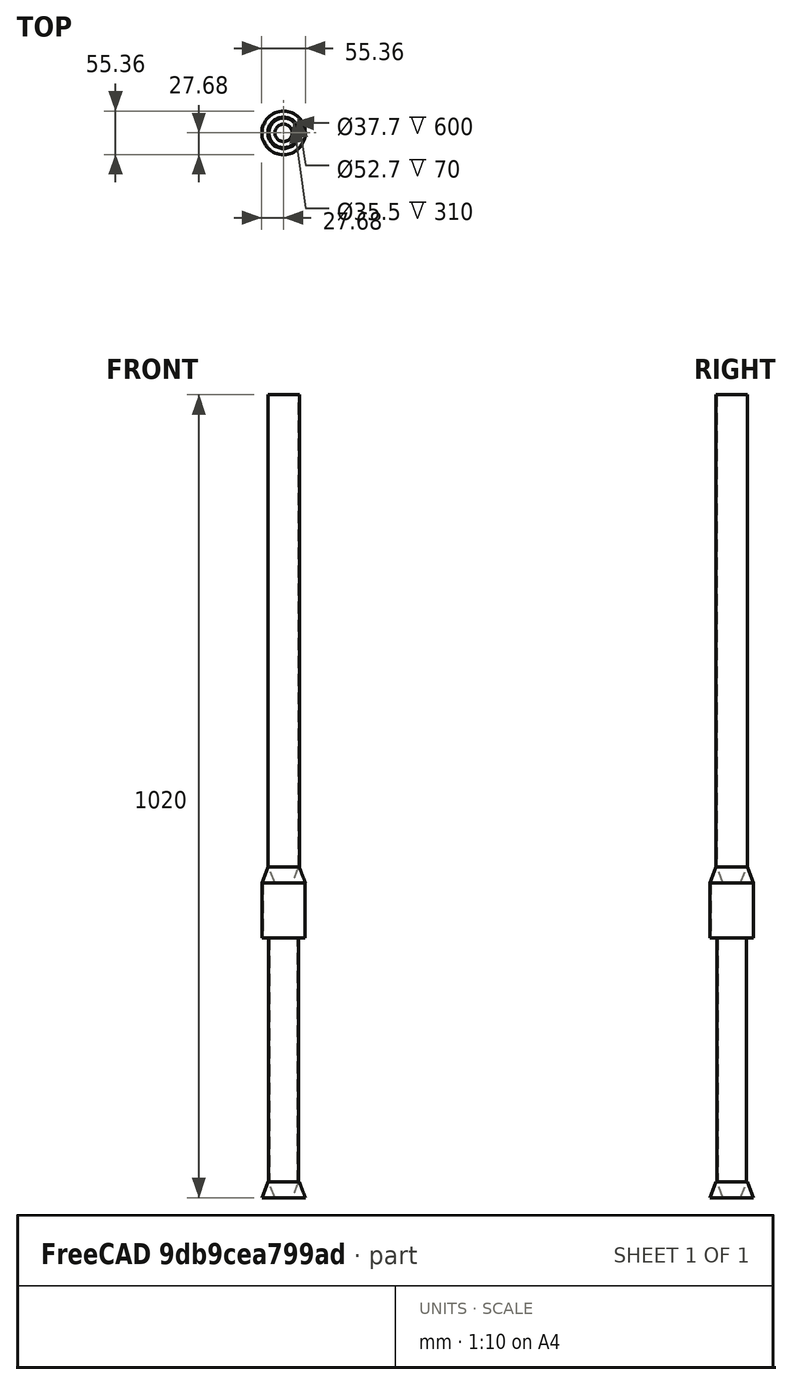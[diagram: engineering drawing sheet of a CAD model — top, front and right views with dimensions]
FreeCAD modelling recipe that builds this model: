
FCSTD DOCUMENT  (FreeCAD 0.21R33771 (Git))
Label: CaneDesign3
License: All rights reserved
LicenseURL: https://en.wikipedia.org/wiki/All_rights_reserved
objects: PartDesign::Body×6, Sketcher::SketchObject×5, PartDesign::Pad×5, App::MeasureDistance×3, Mesh::Feature×1, Spreadsheet::Sheet×1
note: 21 computed .brp shape members not serialized (recipe doc carries the construction recipe); baked Part::Feature solids carry a one-line shape summary decoded from their .brp

FEATURE [Sketcher::SketchObject] Sketch
  FullyConstrained = true
  MapMode = 5
  Support = -> [XY_Plane]
  sketch-geometry (2):
    g0: Circle CenterX=0 CenterY=0 CenterZ=0 NormalX=0 NormalY=0 NormalZ=1 AngleXU=0 Radius=18.9
    g1: Circle CenterX=0 CenterY=0 CenterZ=0 NormalX=0 NormalY=0 NormalZ=1 AngleXU=0 Radius=17.75
  constraints (4):
    c: Coincident(g0,g-1)
    c: Diameter(g0) = 37.8
    c: Coincident(g1,g0)
    c: Diameter(g1) = 35.5
FEATURE [PartDesign::Pad] Pad
  Direction = (0,0,1)
  Length = 310
  Length2 = 10
  Profile = -> Sketch
  ReferenceAxis = -> Sketch [N_Axis]
  Type = 0
FEATURE [PartDesign::Body] Body  label="LegShaft"
  Group = -> [Sketch,Pad]
  Origin = -> Origin
  Placement = pos=(0,0,-160) rot=(0,0,1;0rad)
  Tip = -> Pad
  expr: .Placement.Base.z = <<parameters>>.adjustment_positionz
FEATURE [Sketcher::SketchObject] Sketch001
  FullyConstrained = false
  MapMode = 5
  Support = -> [XY_Plane001]
  sketch-geometry (2):
    g0: Circle CenterX=0 CenterY=0 CenterZ=0 NormalX=0 NormalY=0 NormalZ=1 AngleXU=0 Radius=20
    g1: Circle CenterX=0 CenterY=0 CenterZ=0 NormalX=0 NormalY=0 NormalZ=1 AngleXU=0 Radius=18.85
  constraints (3):
    c: Diameter(g0) = 40
    c: Coincident(g1,g0)
    c: Diameter(g1) = 37.7
FEATURE [PartDesign::Pad] Pad001
  Direction = (0,0,1)
  Length = 600
  Length2 = 10
  Profile = -> Sketch001
  ReferenceAxis = -> Sketch001 [N_Axis]
  Type = 0
FEATURE [PartDesign::Body] Body001  label="ProtectiveCover"
  Group = -> [Sketch001,Pad001]
  Origin = -> Origin001
  Placement = pos=(0,0,240) rot=(0,20,0;0rad)
  Tip = -> Pad001
  expr: .Placement.Rotation.Axis.y = 20
FEATURE [Sketcher::SketchObject] Sketch002
  FullyConstrained = true
  MapMode = 5
  Support = -> [XY_Plane002]
  sketch-geometry (2):
    g0: Circle CenterX=0 CenterY=0 CenterZ=0 NormalX=0 NormalY=0 NormalZ=1 AngleXU=0 Radius=27.5
    g1: Circle CenterX=0 CenterY=0 CenterZ=0 NormalX=0 NormalY=0 NormalZ=1 AngleXU=0 Radius=26.35
  constraints (4):
    c: Coincident(g0,g-1)
    c: Diameter(g0) = 55
    c: Coincident(g1,g0)
    c: Diameter(g1) = 52.7
FEATURE [PartDesign::Pad] Pad002
  Direction = (0,0,1)
  Length = 70
  Length2 = 10
  Profile = -> Sketch002
  ReferenceAxis = -> Sketch002 [N_Axis]
  Type = 0
FEATURE [PartDesign::Body] Body002  label="MotorCover"
  Group = -> [Sketch002,Pad002]
  Origin = -> Origin002
  Placement = pos=(0,0,150) rot=(0,0,1;0rad)
  Tip = -> Pad002
FEATURE [Sketcher::SketchObject] Sketch003
  FullyConstrained = true
  MapMode = 5
  Support = -> [XY_Plane003]
  sketch-geometry (2):
    g0: Circle CenterX=0 CenterY=0 CenterZ=0 NormalX=0 NormalY=0 NormalZ=1 AngleXU=0 Radius=20
    g1: Circle CenterX=0 CenterY=0 CenterZ=0 NormalX=0 NormalY=0 NormalZ=1 AngleXU=0 Radius=18.75
  constraints (4):
    c: Coincident(g0,g-1)
    c: Diameter(g0) = 40
    c: Coincident(g1,g0)
    c: Diameter(g1) = 37.5
FEATURE [PartDesign::Pad] Pad003
  Direction = (0,0,1)
  Length = 20
  Length2 = 10
  Profile = -> Sketch003
  ReferenceAxis = -> Sketch003 [N_Axis]
  Reversed = true
  TaperAngle = 21
  Type = 0
FEATURE [PartDesign::Body] Body003  label="MotorCoverTransition"
  Group = -> [Sketch003,Pad003]
  Origin = -> Origin003
  Placement = pos=(0,0,240) rot=(0,0,1;0rad)
  Tip = -> Pad003
FEATURE [PartDesign::Body] Body004  label="Body"
  Origin = -> Origin004
FEATURE [Mesh::Feature] _7097_Cane_flat_handle_v1_NEW  label="17097_Cane_flat_handle_v1_NEW"
  Placement = pos=(7,10,-69) rot=(0,0,1;1.5708rad)
FEATURE [Sketcher::SketchObject] Sketch005
  FullyConstrained = true
  MapMode = 5
  Support = -> [XY_Plane006]
  sketch-geometry (2):
    g0: Circle CenterX=0 CenterY=0 CenterZ=0 NormalX=0 NormalY=0 NormalZ=1 AngleXU=0 Radius=20
    g1: Circle CenterX=0 CenterY=0 CenterZ=0 NormalX=0 NormalY=0 NormalZ=1 AngleXU=0 Radius=18.75
  constraints (4):
    c: Coincident(g0,g-1)
    c: Diameter(g0) = 40
    c: Coincident(g1,g0)
    c: Diameter(g1) = 37.5
FEATURE [PartDesign::Pad] Pad005
  Direction = (0,0,1)
  Length = 20
  Length2 = 10
  Profile = -> Sketch005
  ReferenceAxis = -> Sketch005 [N_Axis]
  Reversed = true
  TaperAngle = 21
  Type = 0
FEATURE [PartDesign::Body] Body006  label="Foot"
  Group = -> [Sketch005,Pad005]
  Origin = -> Origin006
  Placement = pos=(0,0,-160) rot=(0,0,1;0rad)
  Tip = -> Pad005
  expr: .Placement.Base.z = <<parameters>>.adjustment_positionz
FEATURE [App::MeasureDistance] Distance  label="Distance: 600.16 mm"
  Distance = 600.161
  P1 = (20,0,840)
  P2 = (20.062,0,239.839)
FEATURE [App::MeasureDistance] Distance001  label="Distance: 89.91 mm"
  Distance = 89.9148
  P1 = (20.1483,0,239.614)
  P2 = (27.5,0,150)
FEATURE [App::MeasureDistance] Distance002  label="Distance: 330.00 mm"
  Distance = 330
  P1 = (27.5,0,150)
  P2 = (27.6773,0,-180)
FEATURE [Spreadsheet::Sheet] Spreadsheet  label="parameters"
  cells = B1='measurement; C1='location_z; A2='Height Adjustment; B2(height_adjustment)=310; C2(adjustment_positionz)==-(height_adjustment - 150)
